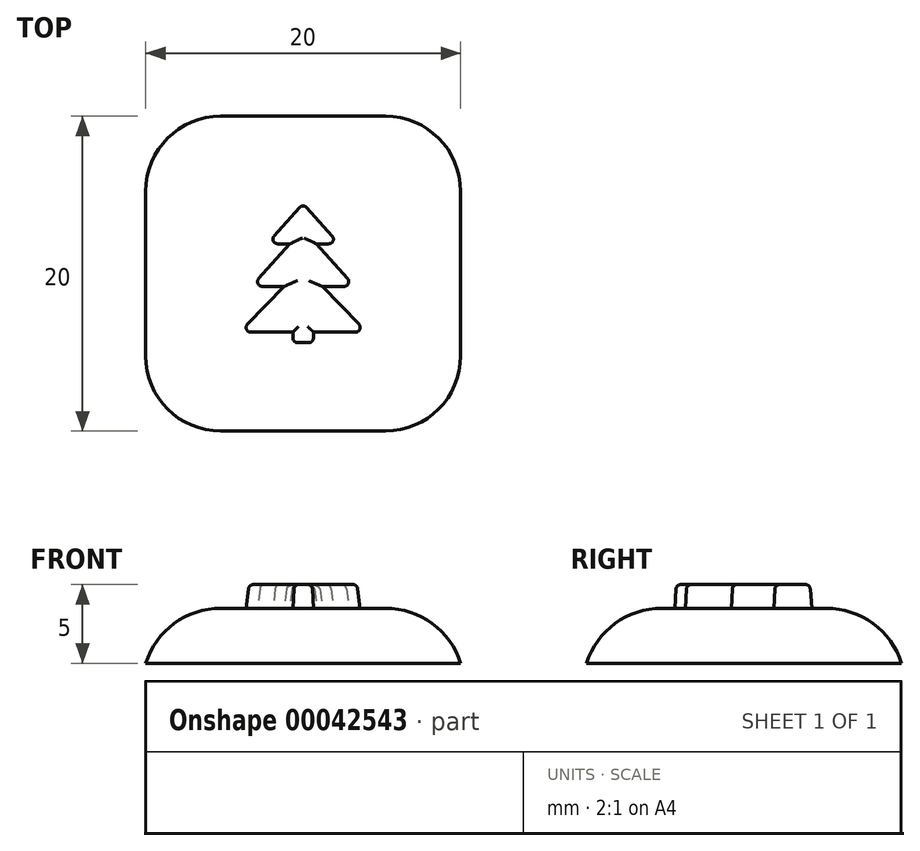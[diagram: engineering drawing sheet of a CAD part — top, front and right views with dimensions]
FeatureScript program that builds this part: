
annotation { "Feature Type Name" : "Feature", "Feature Type Description" : "" }
export const myFeature = defineFeature(function(context is Context, id is Id, definition is map)
    precondition{}
    {
        {
            var Q0;
            Q0=qCreatedBy(makeId("Top.planeOp"),FACE);
            var sketch = newSketch(context, id + "F0", { "sketchPlane" : qUnion([Q0])});
            skLineSegment(sketch, "E0.rect.bottom", {"start": v(10, 10) * mm, "end": v(-10, 10) * mm});
            skLineSegment(sketch, "E0.rect.top", {"start": v(10, -10) * mm, "end": v(-10, -10) * mm});
            skLineSegment(sketch, "E0.rect.left", {"start": v(10, 10) * mm, "end": v(10, -10) * mm});
            skLineSegment(sketch, "E0.rect.right", {"start": v(-10, 10) * mm, "end": v(-10, -10) * mm});
            skPoint(sketch, "E0.rect.middle", {"position": v(0, 0) * mm});
            skSolve(sketch);
        }
        {
            var Q0;
            Q0 = qSketchRegion(id + "F0", true);
            extrude(context, id + "F1", {"entities" : qUnion([Q0]), "depth" : 3.5 * mm, "hasDraft" : true, "draftAngle" : 3 * degree, "draftPullDirection" : true});
        }
        {
            var Q0;
            Q0=makeQuery(id+"F1.opExtrude","CAP_EDGE",EDGE,{"disambiguationData":[OSD([sQuery(id+"F0.wireOp",EDGE,"E0.rect.top")])],"isStart":false});
            var Q1;
            Q1=makeQuery(id+"F1.opExtrude","CAP_EDGE",EDGE,{"disambiguationData":[OSD([sQuery(id+"F0.wireOp",EDGE,"E0.rect.left")])],"isStart":false});
            var Q2;
            Q2=makeQuery(id+"F1.opExtrude","CAP_EDGE",EDGE,{"disambiguationData":[OSD([sQuery(id+"F0.wireOp",EDGE,"E0.rect.bottom")])],"isStart":false});
            var Q3;
            Q3=makeQuery(id+"F1.opExtrude","CAP_EDGE",EDGE,{"disambiguationData":[OSD([sQuery(id+"F0.wireOp",EDGE,"E0.rect.right")])],"isStart":false});
            fillet(context, id + "F2", {"entities" : qUnion([Q0, Q1, Q2, Q3]), "radius" : 5 * mm, "tangentPropagation" : true, "allowEdgeOverflow" : false});
        }
        {
            var Q0;
            Q0=makeQuery(id+"F2.opFillet","BLEND_EDGE",EDGE,{"blendedFrom":[makeQuery(id+"F1.opExtrude","CAP_EDGE",EDGE,{"disambiguationData":[OSD([sQuery(id+"F0.wireOp",EDGE,"E0.rect.top")])],"isStart":false}),makeQuery(id+"F1.opExtrude","CAP_EDGE",EDGE,{"disambiguationData":[OSD([sQuery(id+"F0.wireOp",EDGE,"E0.rect.left")])],"isStart":false})],"blendedInto":[]});
            var Q1;
            Q1=makeQuery(id+"F2.opFillet","BLEND_EDGE",EDGE,{"blendedFrom":[makeQuery(id+"F1.opExtrude","CAP_EDGE",EDGE,{"disambiguationData":[OSD([sQuery(id+"F0.wireOp",EDGE,"E0.rect.bottom")])],"isStart":false}),makeQuery(id+"F1.opExtrude","CAP_EDGE",EDGE,{"disambiguationData":[OSD([sQuery(id+"F0.wireOp",EDGE,"E0.rect.left")])],"isStart":false})],"blendedInto":[]});
            var Q2;
            Q2=makeQuery(id+"F2.opFillet","BLEND_EDGE",EDGE,{"blendedFrom":[makeQuery(id+"F1.opExtrude","CAP_EDGE",EDGE,{"disambiguationData":[OSD([sQuery(id+"F0.wireOp",EDGE,"E0.rect.bottom")])],"isStart":false}),makeQuery(id+"F1.opExtrude","CAP_EDGE",EDGE,{"disambiguationData":[OSD([sQuery(id+"F0.wireOp",EDGE,"E0.rect.right")])],"isStart":false})],"blendedInto":[]});
            var Q3;
            Q3=makeQuery(id+"F2.opFillet","BLEND_EDGE",EDGE,{"blendedFrom":[makeQuery(id+"F1.opExtrude","CAP_EDGE",EDGE,{"disambiguationData":[OSD([sQuery(id+"F0.wireOp",EDGE,"E0.rect.top")])],"isStart":false}),makeQuery(id+"F1.opExtrude","CAP_EDGE",EDGE,{"disambiguationData":[OSD([sQuery(id+"F0.wireOp",EDGE,"E0.rect.right")])],"isStart":false})],"blendedInto":[]});
            fillet(context, id + "F3", {"entities" : qUnion([Q0, Q1, Q2, Q3]), "radius" : 5 * mm, "tangentPropagation" : true, "allowEdgeOverflow" : false});
        }
        {
            var Q0;
            Q0=makeQuery(id+"F1.opExtrude","CAP_FACE",FACE,{"disambiguationData":[OSD([sQuery(id+"F0.wireOp",EDGE,"E0.rect.bottom"),sQuery(id+"F0.wireOp",EDGE,"E0.rect.top"),sQuery(id+"F0.wireOp",EDGE,"E0.rect.left"),sQuery(id+"F0.wireOp",EDGE,"E0.rect.right")])],"isStart":false});
            var sketch = newSketch(context, id + "F4", { "sketchPlane" : qUnion([Q0])});
            skLineSegment(sketch, "E1", {"start": v(0, 4.45) * mm, "end": v(0, -4.38) * mm, "construction": true});
            skPoint(sketch, "E1.startSnap0", {"position": v(0, 5.23) * mm});
            skPoint(sketch, "E1.endSnap0", {"position": v(0, -5.23) * mm});
            skLineSegment(sketch, "E2", {"start": v(0, 4.45) * mm, "end": v(-2.29, 1.9) * mm});
            skLineSegment(sketch, "E3", {"start": v(-2.29, 1.9) * mm, "end": v(-0.86, 1.9) * mm});
            skLineSegment(sketch, "E4", {"start": v(-0.86, 1.9) * mm, "end": v(-3.26, -0.8) * mm});
            skLineSegment(sketch, "E5", {"start": v(-3.26, -0.8) * mm, "end": v(-1.22, -0.8) * mm});
            skLineSegment(sketch, "E6", {"start": v(-1.22, -0.8) * mm, "end": v(-4.03, -3.72) * mm});
            skLineSegment(sketch, "E7", {"start": v(-4.03, -3.72) * mm, "end": v(-0.66, -3.72) * mm});
            skLineSegment(sketch, "E8", {"start": v(-0.66, -3.72) * mm, "end": v(-0.66, -4.38) * mm});
            skLineSegment(sketch, "E9", {"start": v(-0.66, -4.38) * mm, "end": v(0, -4.38) * mm});
            skLineSegment(sketch, "E10.MirrorCS", {"start": v(0, 4.45) * mm, "end": v(2.29, 1.9) * mm});
            skLineSegment(sketch, "E11.MirrorCS", {"start": v(2.29, 1.9) * mm, "end": v(0.86, 1.9) * mm});
            skLineSegment(sketch, "E12.MirrorCS", {"start": v(0.86, 1.9) * mm, "end": v(3.26, -0.8) * mm});
            skLineSegment(sketch, "E13.MirrorCS", {"start": v(3.26, -0.8) * mm, "end": v(1.22, -0.8) * mm});
            skLineSegment(sketch, "E14.MirrorCS", {"start": v(1.22, -0.8) * mm, "end": v(4.03, -3.72) * mm});
            skLineSegment(sketch, "E15.MirrorCS", {"start": v(4.03, -3.72) * mm, "end": v(0.66, -3.72) * mm});
            skLineSegment(sketch, "E16.MirrorCS", {"start": v(0.66, -4.38) * mm, "end": v(0, -4.38) * mm});
            skLineSegment(sketch, "E17.MirrorCS", {"start": v(0.66, -3.72) * mm, "end": v(0.66, -4.38) * mm});
            skSolve(sketch);
        }
        {
            var Q0;
            Q0 = qSketchRegion(id + "F4", true);
            extrude(context, id + "F5", {"entities" : qUnion([Q0]), "operationType" : NewBodyOperationType.ADD, "depth" : 1.5 * mm, "hasDraft" : true, "draftAngle" : 3 * degree, "draftPullDirection" : true});
        }
        {
            var Q0;
            Q0=makeQuery(id+"F5.opExtrude","SWEPT_EDGE",EDGE,{"disambiguationData":[OSD([sQuery(id+"F4.wireOp",EDGE,"E14.MirrorCS"),sQuery(id+"F4.wireOp",EDGE,"E15.MirrorCS")])]});
            var Q1;
            Q1=makeQuery(id+"F5.opExtrude","SWEPT_EDGE",EDGE,{"disambiguationData":[OSD([sQuery(id+"F4.wireOp",EDGE,"E12.MirrorCS"),sQuery(id+"F4.wireOp",EDGE,"E13.MirrorCS")])]});
            var Q2;
            Q2=makeQuery(id+"F5.opExtrude","SWEPT_EDGE",EDGE,{"disambiguationData":[OSD([sQuery(id+"F4.wireOp",EDGE,"E10.MirrorCS"),sQuery(id+"F4.wireOp",EDGE,"E11.MirrorCS")])]});
            var Q3;
            Q3=makeQuery(id+"F5.opExtrude","SWEPT_EDGE",EDGE,{"disambiguationData":[OSD([sQuery(id+"F4.wireOp",EDGE,"E2"),sQuery(id+"F4.wireOp",EDGE,"E3")])]});
            var Q4;
            Q4=makeQuery(id+"F5.opExtrude","SWEPT_EDGE",EDGE,{"disambiguationData":[OSD([sQuery(id+"F4.wireOp",EDGE,"E4"),sQuery(id+"F4.wireOp",EDGE,"E5")])]});
            var Q5;
            Q5=makeQuery(id+"F5.opExtrude","SWEPT_EDGE",EDGE,{"disambiguationData":[OSD([sQuery(id+"F4.wireOp",EDGE,"E6"),sQuery(id+"F4.wireOp",EDGE,"E7")])]});
            var Q6;
            Q6=makeQuery(id+"F5.opExtrude","SWEPT_EDGE",EDGE,{"disambiguationData":[OSD([sQuery(id+"F4.wireOp",EDGE,"E16.MirrorCS"),sQuery(id+"F4.wireOp",EDGE,"E17.MirrorCS")])]});
            var Q7;
            Q7=makeQuery(id+"F5.opExtrude","SWEPT_EDGE",EDGE,{"disambiguationData":[OSD([sQuery(id+"F4.wireOp",EDGE,"E8"),sQuery(id+"F4.wireOp",EDGE,"E9")])]});
            var Q8;
            Q8=makeQuery(id+"F5.opExtrude","SWEPT_EDGE",EDGE,{"disambiguationData":[OSD([sQuery(id+"F4.wireOp",EDGE,"E2"),sQuery(id+"F4.wireOp",EDGE,"E10.MirrorCS")])]});
            fillet(context, id + "F6", {"entities" : qUnion([Q0, Q1, Q2, Q3, Q4, Q5, Q6, Q7, Q8]), "radius" : 0.3 * mm, "tangentPropagation" : true, "allowEdgeOverflow" : false});
        }
        {
            var Q0;
            Q0=makeQuery(id+"F5.opExtrude","CAP_FACE",FACE,{"disambiguationData":[OSD([sQuery(id+"F4.wireOp",EDGE,"E2"),sQuery(id+"F4.wireOp",EDGE,"E3"),sQuery(id+"F4.wireOp",EDGE,"E4"),sQuery(id+"F4.wireOp",EDGE,"E5"),sQuery(id+"F4.wireOp",EDGE,"E6"),sQuery(id+"F4.wireOp",EDGE,"E7"),sQuery(id+"F4.wireOp",EDGE,"E8"),sQuery(id+"F4.wireOp",EDGE,"E9"),sQuery(id+"F4.wireOp",EDGE,"E10.MirrorCS"),sQuery(id+"F4.wireOp",EDGE,"E11.MirrorCS"),sQuery(id+"F4.wireOp",EDGE,"E12.MirrorCS"),sQuery(id+"F4.wireOp",EDGE,"E13.MirrorCS"),sQuery(id+"F4.wireOp",EDGE,"E14.MirrorCS"),sQuery(id+"F4.wireOp",EDGE,"E15.MirrorCS"),sQuery(id+"F4.wireOp",EDGE,"E16.MirrorCS"),sQuery(id+"F4.wireOp",EDGE,"E17.MirrorCS")])],"isStart":false});
            fillet(context, id + "F7", {"entities" : qUnion([Q0]), "radius" : 0.3 * mm, "tangentPropagation" : true, "allowEdgeOverflow" : false});
        }
    });
